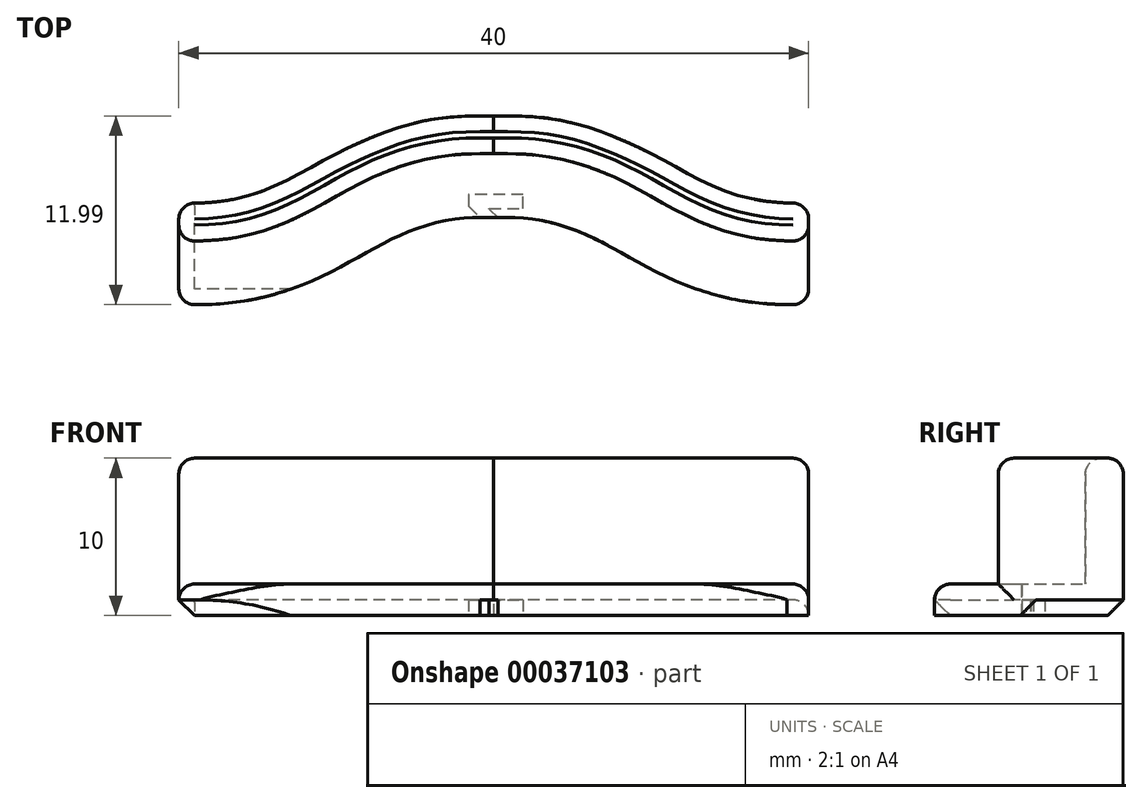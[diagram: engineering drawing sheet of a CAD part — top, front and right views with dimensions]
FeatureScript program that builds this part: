
annotation { "Feature Type Name" : "Feature", "Feature Type Description" : "" }
export const myFeature = defineFeature(function(context is Context, id is Id, definition is map)
    precondition{}
    {
        {
            var Q0;
            Q0=qCreatedBy(makeId("Top.planeOp"),FACE);
            var sketch = newSketch(context, id + "F0", { "sketchPlane" : qUnion([Q0]), "disableImprinting" : false});
            skLineSegment(sketch, "E0.bottom", {"start": v(-20, 0) * mm, "end": v(20, 0) * mm});
            skLineSegment(sketch, "E0.left", {"start": v(-20, 0) * mm, "end": v(-20, 6.45) * mm});
            skLineSegment(sketch, "E0.right", {"start": v(20, 0) * mm, "end": v(20, 6.45) * mm});
            skLineSegment(sketch, "E1", {"start": v(0, 0) * mm, "end": v(0, 11.98) * mm, "construction": true});
            skFitSpline(sketch, "E2", {"points": [v(-20, 2.4) * mm, v(0, 7.93) * mm], "startDerivative": vector(30.52, 0) * mm, "endDerivative": vector(27.9, 0) * mm});
            skFitSpline(sketch, "E3.MirrorCS", {"points": [v(20, 2.4) * mm, v(0, 7.93) * mm], "startDerivative": vector(-30.52, 0) * mm, "endDerivative": vector(-27.9, 0) * mm});
            skFitSpline(sketch, "E4.0", {"points": [v(20, 4.05) * mm, v(18.8, 4.05) * mm, v(16.73, 4.21) * mm, v(14.32, 4.8) * mm, v(12.33, 5.62) * mm, v(10.47, 6.6) * mm, v(8.5, 7.68) * mm, v(6.23, 8.68) * mm, v(3.48, 9.4) * mm, v(1.24, 9.58) * mm, v(0, 9.58) * mm]});
            skFitSpline(sketch, "E4.1", {"points": [v(-20, 4.05) * mm, v(-18.8, 4.05) * mm, v(-16.73, 4.21) * mm, v(-14.32, 4.8) * mm, v(-12.33, 5.62) * mm, v(-10.47, 6.6) * mm, v(-8.5, 7.68) * mm, v(-6.23, 8.68) * mm, v(-3.48, 9.4) * mm, v(-1.24, 9.58) * mm, v(0, 9.58) * mm]});
            skFitSpline(sketch, "E5.0", {"points": [v(20, 6.45) * mm, v(18.91, 6.45) * mm, v(17.08, 6.6) * mm, v(15.07, 7.1) * mm, v(13.38, 7.78) * mm, v(11.94, 8.55) * mm, v(10.62, 9.26) * mm, v(9.53, 9.82) * mm, v(8.31, 10.39) * mm, v(6.5, 11.09) * mm, v(3.87, 11.78) * mm, v(1.36, 11.98) * mm, v(0, 11.98) * mm]});
            skFitSpline(sketch, "E5.1", {"points": [v(-20, 6.45) * mm, v(-18.91, 6.45) * mm, v(-17.08, 6.6) * mm, v(-15.07, 7.1) * mm, v(-13.38, 7.78) * mm, v(-11.94, 8.55) * mm, v(-10.62, 9.26) * mm, v(-9.53, 9.82) * mm, v(-8.31, 10.39) * mm, v(-6.5, 11.09) * mm, v(-3.87, 11.78) * mm, v(-1.36, 11.98) * mm, v(0, 11.98) * mm]});
            skFitSpline(sketch, "E6.0", {"points": [v(20, 0) * mm, v(18.62, 0) * mm, v(16.13, 0.19) * mm, v(13.07, 0.93) * mm, v(10.56, 1.97) * mm, v(8.5, 3.07) * mm, v(6.67, 4.06) * mm, v(4.89, 4.84) * mm, v(2.83, 5.38) * mm, v(1.04, 5.53) * mm, v(0, 5.53) * mm]});
            skFitSpline(sketch, "E6.1", {"points": [v(-20, 0) * mm, v(-18.62, 0) * mm, v(-16.13, 0.19) * mm, v(-13.07, 0.93) * mm, v(-10.56, 1.97) * mm, v(-8.5, 3.07) * mm, v(-6.67, 4.06) * mm, v(-4.89, 4.84) * mm, v(-2.83, 5.38) * mm, v(-1.04, 5.53) * mm, v(0, 5.53) * mm]});
            skSolve(sketch);
        }
        {
            var Q0;
            Q0=makeQuery(id+"F0.imprint","IMPRINT",FACE,{"disambiguationData":[TD([[makeQuery(id+"F0.imprint","IMPRINT",EDGE,{"derivedFrom":sQuery(id+"F0.wireOp",EDGE,"E0.bottom")}),1.0]])]});
            var Q1;
            {var subQ3=sQuery(id+"F0.wireOp",EDGE,"E2");Q1=makeQuery(id+"F0.imprint","IMPRINT",FACE,{"disambiguationData":[TD([[makeQuery(id+"F0.imprint","IMPRINT",EDGE,{"derivedFrom":subQ3}),-1.0]])]});}
            var Q2;
            {var subQ3=sQuery(id+"F0.wireOp",EDGE,"E2");Q2=makeQuery(id+"F0.imprint","IMPRINT",FACE,{"disambiguationData":[TD([[makeQuery(id+"F0.imprint","IMPRINT",EDGE,{"derivedFrom":subQ3}),1.0]])]});}
            var Q3;
            {var subQ2=sQuery(id+"F0.wireOp",EDGE,"E4.0");Q3=makeQuery(id+"F0.imprint","IMPRINT",FACE,{"disambiguationData":[TD([[makeQuery(id+"F0.imprint","IMPRINT",EDGE,{"derivedFrom":subQ2}),-1.0]])]});}
            extrude(context, id + "F1", {"entities" : qUnion([Q0, Q1, Q2, Q3]), "depth" : 2 * mm});
        }
        {
            var Q0;
            {var subQ3=sQuery(id+"F0.wireOp",EDGE,"E2");Q0=makeQuery(id+"F0.imprint","IMPRINT",FACE,{"disambiguationData":[TD([[makeQuery(id+"F0.imprint","IMPRINT",EDGE,{"derivedFrom":subQ3}),-1.0]])]});}
            var Q1;
            {var subQ2=sQuery(id+"F0.wireOp",EDGE,"E4.0");Q1=makeQuery(id+"F0.imprint","IMPRINT",FACE,{"disambiguationData":[TD([[makeQuery(id+"F0.imprint","IMPRINT",EDGE,{"derivedFrom":subQ2}),-1.0]])]});}
            extrude(context, id + "F2", {"entities" : qUnion([Q0, Q1]), "operationType" : NewBodyOperationType.ADD, "depth" : 10 * mm});
        }
        {
            var Q0;
            Q0=makeQuery(id+"F2.opExtrude","CAP_EDGE",EDGE,{"disambiguationData":[OSD([sQuery(id+"F0.wireOp",EDGE,"E5.1")])],"isStart":false});
            var Q1;
            Q1=makeQuery(id+"F2.opExtrude","CAP_EDGE",EDGE,{"disambiguationData":[OSD([sQuery(id+"F0.wireOp",EDGE,"E5.0")])],"isStart":false});
            var Q2;
            Q2=makeQuery(id+"F2.opExtrude","CAP_EDGE",EDGE,{"disambiguationData":[OSD([sQuery(id+"F0.wireOp",EDGE,"E4.1")])],"isStart":false});
            var Q3;
            Q3=makeQuery(id+"F2.opExtrude","CAP_EDGE",EDGE,{"disambiguationData":[OSD([sQuery(id+"F0.wireOp",EDGE,"E4.0")])],"isStart":false});
            var Q4;
            Q4=makeQuery(id+"F2.opExtrude","CAP_EDGE",EDGE,{"disambiguationData":[OSD([sQuery(id+"F0.wireOp",EDGE,"E2")])],"isStart":false});
            var Q5;
            Q5=makeQuery(id+"F2.opExtrude","CAP_EDGE",EDGE,{"disambiguationData":[OSD([sQuery(id+"F0.wireOp",EDGE,"E3.MirrorCS")])],"isStart":false});
            var Q6;
            Q6=makeQuery(id+"F2.opExtrude","CAP_EDGE",EDGE,{"disambiguationData":[OSD([sQuery(id+"F0.wireOp",EDGE,"E6.1")])],"isStart":false});
            var Q7;
            Q7=makeQuery(id+"F2.opExtrude","CAP_EDGE",EDGE,{"disambiguationData":[OSD([sQuery(id+"F0.wireOp",EDGE,"E6.0")])],"isStart":false});
            var Q8;
            {var subQ0=sQuery(id+"F0.wireOp",EDGE,"E0.left");Q8=makeQuery(id+"F2.opExtrude","CAP_EDGE",EDGE,{"disambiguationData":[OSD([subQ0]),TDD([makeQuery(id+"F0.imprint","IMPRINT",EDGE,{"disambiguationData":[TD([[makeQuery(id+"F0.imprint","INTERSECT",VERTEX,{"derivedFrom":[subQ0,sQuery(id+"F0.wireOp",EDGE,"E5.1")]}),1.0]])],"derivedFrom":subQ0})])],"isStart":false});}
            var Q9;
            {var subQ0=sQuery(id+"F0.wireOp",EDGE,"E0.left");Q9=makeQuery(id+"F2.opExtrude","CAP_EDGE",EDGE,{"disambiguationData":[OSD([subQ0]),TDD([makeQuery(id+"F0.imprint","IMPRINT",EDGE,{"disambiguationData":[TD([[makeQuery(id+"F0.imprint","INTERSECT",VERTEX,{"derivedFrom":[subQ0,sQuery(id+"F0.wireOp",EDGE,"E2")]}),1.0]])],"derivedFrom":subQ0})])],"isStart":false});}
            var Q10;
            {var subQ0=sQuery(id+"F0.wireOp",EDGE,"E0.right");Q10=makeQuery(id+"F2.opExtrude","CAP_EDGE",EDGE,{"disambiguationData":[OSD([subQ0]),TDD([makeQuery(id+"F0.imprint","IMPRINT",EDGE,{"disambiguationData":[TD([[makeQuery(id+"F0.imprint","INTERSECT",VERTEX,{"derivedFrom":[subQ0,sQuery(id+"F0.wireOp",EDGE,"E3.MirrorCS")]}),1.0]])],"derivedFrom":subQ0})])],"isStart":false});}
            var Q11;
            {var subQ0=sQuery(id+"F0.wireOp",EDGE,"E0.right");Q11=makeQuery(id+"F2.opExtrude","CAP_EDGE",EDGE,{"disambiguationData":[OSD([subQ0]),TDD([makeQuery(id+"F0.imprint","IMPRINT",EDGE,{"disambiguationData":[TD([[makeQuery(id+"F0.imprint","INTERSECT",VERTEX,{"derivedFrom":[subQ0,sQuery(id+"F0.wireOp",EDGE,"E5.0")]}),1.0]])],"derivedFrom":subQ0})])],"isStart":false});}
            var Q12;
            {var subQ0=sQuery(id+"F0.wireOp",EDGE,"E0.left");var subQ1=sQuery(id+"F0.wireOp",EDGE,"E5.1");Q12=makeQuery(id+"F2.boolean.opBoolean","MERGE",EDGE,{"derivedFrom":[makeQuery(id+"F1.opExtrude","SWEPT_EDGE",EDGE,{"disambiguationData":[OSD([subQ0,subQ1])]}),makeQuery(id+"F2.opExtrude","SWEPT_EDGE",EDGE,{"disambiguationData":[OSD([subQ0,subQ1])]})]});}
            var Q13;
            Q13=makeQuery(id+"F2.opExtrude","SWEPT_EDGE",EDGE,{"disambiguationData":[OSD([sQuery(id+"F0.wireOp",EDGE,"E0.left"),sQuery(id+"F0.wireOp",EDGE,"E2")])]});
            var Q14;
            Q14=makeQuery(id+"F2.opExtrude","SWEPT_EDGE",EDGE,{"disambiguationData":[OSD([sQuery(id+"F0.wireOp",EDGE,"E0.left"),sQuery(id+"F0.wireOp",EDGE,"E4.1")])]});
            var Q15;
            Q15=makeQuery(id+"F1.opExtrude","SWEPT_EDGE",EDGE,{"disambiguationData":[OSD([sQuery(id+"F0.wireOp",EDGE,"E0.bottom"),sQuery(id+"F0.wireOp",EDGE,"E0.left"),sQuery(id+"F0.wireOp",EDGE,"E6.1")])]});
            var Q16;
            {var subQ0=sQuery(id+"F0.wireOp",EDGE,"E0.right");var subQ1=sQuery(id+"F0.wireOp",EDGE,"E5.0");Q16=makeQuery(id+"F2.boolean.opBoolean","MERGE",EDGE,{"derivedFrom":[makeQuery(id+"F1.opExtrude","SWEPT_EDGE",EDGE,{"disambiguationData":[OSD([subQ0,subQ1])]}),makeQuery(id+"F2.opExtrude","SWEPT_EDGE",EDGE,{"disambiguationData":[OSD([subQ0,subQ1])]})]});}
            var Q17;
            Q17=makeQuery(id+"F2.opExtrude","SWEPT_EDGE",EDGE,{"disambiguationData":[OSD([sQuery(id+"F0.wireOp",EDGE,"E0.right"),sQuery(id+"F0.wireOp",EDGE,"E3.MirrorCS")])]});
            var Q18;
            Q18=makeQuery(id+"F2.opExtrude","SWEPT_EDGE",EDGE,{"disambiguationData":[OSD([sQuery(id+"F0.wireOp",EDGE,"E0.right"),sQuery(id+"F0.wireOp",EDGE,"E4.0")])]});
            var Q19;
            Q19=makeQuery(id+"F1.opExtrude","SWEPT_EDGE",EDGE,{"disambiguationData":[OSD([sQuery(id+"F0.wireOp",EDGE,"E0.bottom"),sQuery(id+"F0.wireOp",EDGE,"E0.right"),sQuery(id+"F0.wireOp",EDGE,"E6.0")])]});
            var Q20;
            Q20=makeQuery(id+"F2.boolean.opBoolean","INTERSECT",EDGE,{"derivedFrom":[makeQuery(id+"F1.opExtrude","CAP_FACE",FACE,{"disambiguationData":[OSD([sQuery(id+"F0.wireOp",EDGE,"E0.bottom"),sQuery(id+"F0.wireOp",EDGE,"E0.left"),sQuery(id+"F0.wireOp",EDGE,"E0.right"),sQuery(id+"F0.wireOp",EDGE,"E5.0"),sQuery(id+"F0.wireOp",EDGE,"E5.1")])],"isStart":false}),makeQuery(id+"F2.opExtrude","SWEPT_FACE",FACE,{"disambiguationData":[OSD([sQuery(id+"F0.wireOp",EDGE,"E6.1")])]})]});
            var Q21;
            Q21=makeQuery(id+"F2.boolean.opBoolean","INTERSECT",EDGE,{"derivedFrom":[makeQuery(id+"F1.opExtrude","CAP_FACE",FACE,{"disambiguationData":[OSD([sQuery(id+"F0.wireOp",EDGE,"E0.bottom"),sQuery(id+"F0.wireOp",EDGE,"E0.left"),sQuery(id+"F0.wireOp",EDGE,"E0.right"),sQuery(id+"F0.wireOp",EDGE,"E5.0"),sQuery(id+"F0.wireOp",EDGE,"E5.1")])],"isStart":false}),makeQuery(id+"F2.opExtrude","SWEPT_FACE",FACE,{"disambiguationData":[OSD([sQuery(id+"F0.wireOp",EDGE,"E6.0")])]})]});
            fillet(context, id + "F3", {"entities" : qUnion([Q0, Q1, Q2, Q3, Q4, Q5, Q6, Q7, Q8, Q9, Q10, Q11, Q12, Q13, Q14, Q15, Q16, Q17, Q18, Q19, Q20, Q21]), "radius" : 1 * mm, "tangentPropagation" : true, "allowEdgeOverflow" : false});
        }
        {
            var Q0;
            Q0=makeQuery(id+"F1.opExtrude","CAP_EDGE",EDGE,{"disambiguationData":[OSD([sQuery(id+"F0.wireOp",EDGE,"E0.bottom")])],"isStart":false});
            fillet(context, id + "F4", {"entities" : qUnion([Q0]), "radius" : 1 * mm, "tangentPropagation" : true, "allowEdgeOverflow" : false});
        }
        {
            var Q0;
            Q0=makeQuery(id+"F1.opExtrude","CAP_FACE",FACE,{"disambiguationData":[OSD([sQuery(id+"F0.wireOp",EDGE,"E0.bottom"),sQuery(id+"F0.wireOp",EDGE,"E0.left"),sQuery(id+"F0.wireOp",EDGE,"E0.right"),sQuery(id+"F0.wireOp",EDGE,"E5.0"),sQuery(id+"F0.wireOp",EDGE,"E5.1")])],"isStart":true});
            var sketch = newSketch(context, id + "F5", { "sketchPlane" : qUnion([Q0])});
            skText(sketch, "E7", { "text": "2", "fontName": "OpenSans-Bold.ttf"});
            const initialGuessF5  = {"E7": [-0.00187, -0.007, 1, 0, 0.005]};
            skSetInitialGuess(sketch, initialGuessF5);
            skSolve(sketch);
        }
        {
            var Q0;
            Q0=qSketchRegion(id+"F5",true);
            extrude(context, id + "F6", {"entities" : qUnion([Q0]), "operationType" : NewBodyOperationType.REMOVE, "oppositeDirection" : true, "depth" : 1 * mm});
        }
        {
            var Q0;
            {var subQ0=sQuery(id+"F0.wireOp",EDGE,"E0.left");var subQ1=sQuery(id+"F0.wireOp",EDGE,"E0.bottom");Q0=makeQuery(id+"F3.opFillet","BLEND_EDGE",EDGE,{"blendedFrom":[makeQuery(id+"F1.opExtrude","SWEPT_EDGE",EDGE,{"disambiguationData":[OSD([subQ1,subQ0,sQuery(id+"F0.wireOp",EDGE,"E6.1")])]}),makeQuery(id+"F1.opExtrude","CAP_FACE",FACE,{"disambiguationData":[OSD([subQ1,subQ0,sQuery(id+"F0.wireOp",EDGE,"E0.right"),sQuery(id+"F0.wireOp",EDGE,"E5.0"),sQuery(id+"F0.wireOp",EDGE,"E5.1")])],"isStart":true})],"blendedInto":[makeQuery(id+"F1.opExtrude","CAP_FACE",FACE,{"disambiguationData":[OSD([subQ1,subQ0,sQuery(id+"F0.wireOp",EDGE,"E0.right"),sQuery(id+"F0.wireOp",EDGE,"E5.0"),sQuery(id+"F0.wireOp",EDGE,"E5.1")])],"isStart":true})]});}
            chamfer(context, id + "F7", {"entities" : qUnion([Q0]), "width" : 1 * mm, "tangentPropagation" : true});
        }
    });
